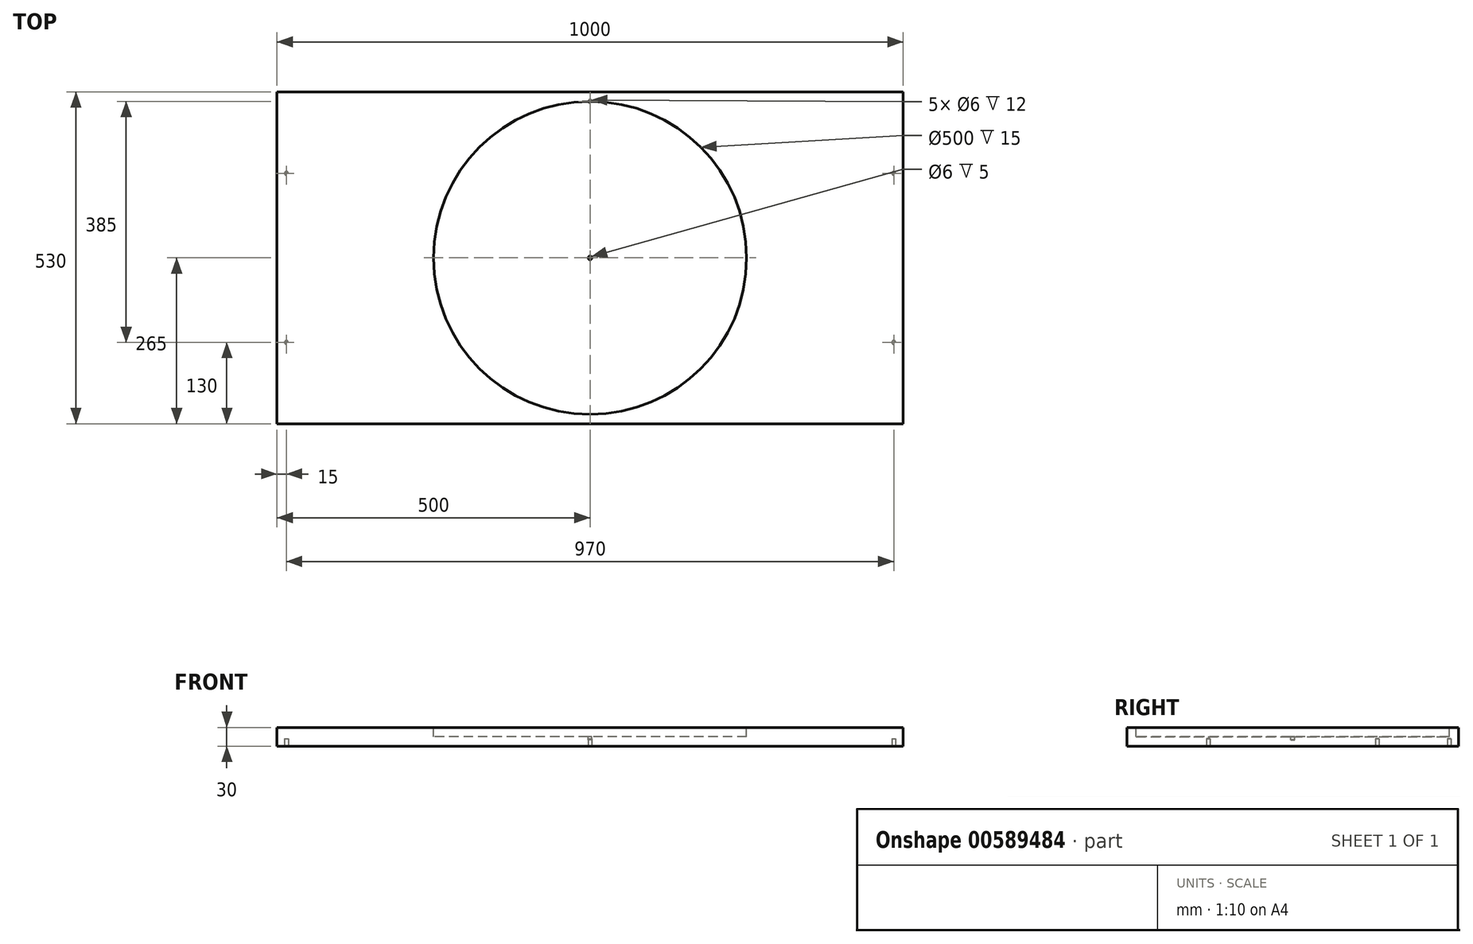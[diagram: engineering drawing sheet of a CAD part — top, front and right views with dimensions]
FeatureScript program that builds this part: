
annotation { "Feature Type Name" : "Feature", "Feature Type Description" : "" }
export const myFeature = defineFeature(function(context is Context, id is Id, definition is map)
    precondition{}
    {
        {
            var Q0;
            Q0=qCreatedBy(makeId("Top.planeOp"),FACE);
            var sketch = newSketch(context, id + "F0", { "sketchPlane" : qUnion([Q0])});
            skLineSegment(sketch, "E0.bottom", {"start": v(0, 0) * mm, "end": v(1000, 0) * mm});
            skLineSegment(sketch, "E0.top", {"start": v(0, 530) * mm, "end": v(1000, 530) * mm});
            skLineSegment(sketch, "E0.left", {"start": v(0, 0) * mm, "end": v(0, 530) * mm});
            skLineSegment(sketch, "E0.right", {"start": v(1000, 0) * mm, "end": v(1000, 530) * mm});
            skSolve(sketch);
        }
        {
            var Q0;
            Q0=makeQuery(id+"F0.imprint","IMPRINT",FACE,{"disambiguationData":[TD([[makeQuery(id+"F0.imprint","IMPRINT",EDGE,{"derivedFrom":sQuery(id+"F0.wireOp",EDGE,"E0.bottom")}),1.0]])]});
            extrude(context, id + "F1", {"entities" : qUnion([Q0]), "depth" : 30 * mm, "offsetDistance" : 25 * mm});
        }
        {
            var Q0;
            Q0=makeQuery(id+"F1.opExtrude","CAP_FACE",FACE,{"disambiguationData":[OSD([sQuery(id+"F0.wireOp",EDGE,"E0.bottom"),sQuery(id+"F0.wireOp",EDGE,"E0.top"),sQuery(id+"F0.wireOp",EDGE,"E0.left"),sQuery(id+"F0.wireOp",EDGE,"E0.right")])],"isStart":true});
            var sketch = newSketch(context, id + "F2", { "sketchPlane" : qUnion([Q0])});
            skCircle(sketch, "E1", {"center": v(985, -130) * mm, "radius": 3 * mm});
            skSolve(sketch);
        }
        {
            var Q0;
            Q0=makeQuery(id+"F2.imprint","IMPRINT",FACE,{"disambiguationData":[TD([[makeQuery(id+"F2.imprint","IMPRINT",EDGE,{"derivedFrom":sQuery(id+"F2.wireOp",EDGE,"E1")}),1.0]])]});
            extrude(context, id + "F3", {"entities" : qUnion([Q0]), "operationType" : NewBodyOperationType.REMOVE, "oppositeDirection" : true, "depth" : 12 * mm, "offsetDistance" : 25 * mm});
        }
        {
            var Q0;
            Q0=makeQuery(id+"F1.opExtrude","CAP_FACE",FACE,{"disambiguationData":[OSD([sQuery(id+"F0.wireOp",EDGE,"E0.bottom"),sQuery(id+"F0.wireOp",EDGE,"E0.top"),sQuery(id+"F0.wireOp",EDGE,"E0.left"),sQuery(id+"F0.wireOp",EDGE,"E0.right")])],"isStart":true});
            var sketch = newSketch(context, id + "F4", { "sketchPlane" : qUnion([Q0])});
            skCircle(sketch, "E2", {"center": v(15, -130) * mm, "radius": 3 * mm});
            skCircle(sketch, "E3", {"center": v(15, -400) * mm, "radius": 3 * mm});
            skSolve(sketch);
        }
        {
            var Q0;
            Q0=makeQuery(id+"F4.imprint","IMPRINT",FACE,{"disambiguationData":[TD([[makeQuery(id+"F4.imprint","IMPRINT",EDGE,{"derivedFrom":sQuery(id+"F4.wireOp",EDGE,"E2")}),1.0]])]});
            extrude(context, id + "F5", {"entities" : qUnion([Q0]), "operationType" : NewBodyOperationType.REMOVE, "oppositeDirection" : true, "depth" : 12 * mm, "offsetDistance" : 25 * mm});
        }
        {
            var Q0;
            Q0=makeQuery(id+"F1.opExtrude","CAP_FACE",FACE,{"disambiguationData":[OSD([sQuery(id+"F0.wireOp",EDGE,"E0.bottom"),sQuery(id+"F0.wireOp",EDGE,"E0.top"),sQuery(id+"F0.wireOp",EDGE,"E0.left"),sQuery(id+"F0.wireOp",EDGE,"E0.right")])],"isStart":false});
            var sketch = newSketch(context, id + "F6", { "sketchPlane" : qUnion([Q0])});
            skCircle(sketch, "E4", {"center": v(500, 265) * mm, "radius": 250 * mm});
            skPoint(sketch, "E4.centerSnap0", {"position": v(0, 265) * mm});
            skPoint(sketch, "E4.centerSnap1", {"position": v(500, 530) * mm});
            skSolve(sketch);
        }
        {
            var Q0;
            Q0=makeQuery(id+"F1.opExtrude","CAP_FACE",FACE,{"disambiguationData":[OSD([sQuery(id+"F0.wireOp",EDGE,"E0.bottom"),sQuery(id+"F0.wireOp",EDGE,"E0.top"),sQuery(id+"F0.wireOp",EDGE,"E0.left"),sQuery(id+"F0.wireOp",EDGE,"E0.right")])],"isStart":true});
            var sketch = newSketch(context, id + "F7", { "sketchPlane" : qUnion([Q0])});
            skCircle(sketch, "E5", {"center": v(985, -400) * mm, "radius": 3 * mm});
            skSolve(sketch);
        }
        {
            var Q0;
            Q0=makeQuery(id+"F7.imprint","IMPRINT",FACE,{"disambiguationData":[TD([[makeQuery(id+"F7.imprint","IMPRINT",EDGE,{"derivedFrom":sQuery(id+"F7.wireOp",EDGE,"E5")}),1.0]])]});
            extrude(context, id + "F8", {"entities" : qUnion([Q0]), "operationType" : NewBodyOperationType.REMOVE, "oppositeDirection" : true, "depth" : 12 * mm, "offsetDistance" : 25 * mm});
        }
        {
            var Q0;
            Q0=makeQuery(id+"F1.opExtrude","CAP_FACE",FACE,{"disambiguationData":[OSD([sQuery(id+"F0.wireOp",EDGE,"E0.bottom"),sQuery(id+"F0.wireOp",EDGE,"E0.top"),sQuery(id+"F0.wireOp",EDGE,"E0.left"),sQuery(id+"F0.wireOp",EDGE,"E0.right")])],"isStart":true});
            var sketch = newSketch(context, id + "F9", { "sketchPlane" : qUnion([Q0])});
            skCircle(sketch, "E6", {"center": v(15, -400) * mm, "radius": 3 * mm});
            skSolve(sketch);
        }
        {
            var Q0;
            Q0=makeQuery(id+"F9.imprint","IMPRINT",FACE,{"disambiguationData":[TD([[makeQuery(id+"F9.imprint","IMPRINT",EDGE,{"derivedFrom":sQuery(id+"F9.wireOp",EDGE,"E6")}),1.0]])]});
            extrude(context, id + "F10", {"entities" : qUnion([Q0]), "operationType" : NewBodyOperationType.REMOVE, "oppositeDirection" : true, "depth" : 12 * mm, "offsetDistance" : 25 * mm});
        }
        {
            var Q0;
            Q0=makeQuery(id+"F6.imprint","IMPRINT",FACE,{"disambiguationData":[TD([[makeQuery(id+"F6.imprint","IMPRINT",EDGE,{"derivedFrom":sQuery(id+"F6.wireOp",EDGE,"E4")}),1.0]])]});
            extrude(context, id + "F11", {"entities" : qUnion([Q0]), "operationType" : NewBodyOperationType.REMOVE, "oppositeDirection" : true, "depth" : 15 * mm, "offsetDistance" : 25 * mm});
        }
        {
            var Q0;
            Q0=makeQuery(id+"F11.boolean.opBoolean","COPY",FACE,{"derivedFrom":makeQuery(id+"F11.opExtrude","CAP_FACE",FACE,{"disambiguationData":[OSD([sQuery(id+"F6.wireOp",EDGE,"E4")])],"isStart":false})});
            var sketch = newSketch(context, id + "F12", { "sketchPlane" : qUnion([Q0])});
            skCircle(sketch, "E7", {"center": v(500, 265) * mm, "radius": 3 * mm});
            skSolve(sketch);
        }
        {
            var Q0;
            Q0=makeQuery(id+"F12.imprint","IMPRINT",FACE,{"disambiguationData":[TD([[makeQuery(id+"F12.imprint","IMPRINT",EDGE,{"derivedFrom":sQuery(id+"F12.wireOp",EDGE,"E7")}),1.0]])]});
            extrude(context, id + "F13", {"entities" : qUnion([Q0]), "operationType" : NewBodyOperationType.REMOVE, "oppositeDirection" : true, "depth" : 5 * mm, "offsetDistance" : 25 * mm});
        }
        {
            var Q0;
            Q0=makeQuery(id+"F1.opExtrude","CAP_FACE",FACE,{"disambiguationData":[OSD([sQuery(id+"F0.wireOp",EDGE,"E0.bottom"),sQuery(id+"F0.wireOp",EDGE,"E0.top"),sQuery(id+"F0.wireOp",EDGE,"E0.left"),sQuery(id+"F0.wireOp",EDGE,"E0.right")])],"isStart":true});
            var sketch = newSketch(context, id + "F14", { "sketchPlane" : qUnion([Q0])});
            skCircle(sketch, "E8", {"center": v(500, -515) * mm, "radius": 3 * mm});
            skPoint(sketch, "E8.centerSnap0", {"position": v(500, -530) * mm});
            skSolve(sketch);
        }
        {
            var Q0;
            Q0=makeQuery(id+"F14.imprint","IMPRINT",FACE,{"disambiguationData":[TD([[makeQuery(id+"F14.imprint","IMPRINT",EDGE,{"derivedFrom":sQuery(id+"F14.wireOp",EDGE,"E8")}),1.0]])]});
            extrude(context, id + "F15", {"entities" : qUnion([Q0]), "operationType" : NewBodyOperationType.REMOVE, "oppositeDirection" : true, "depth" : 12 * mm, "offsetDistance" : 25 * mm});
        }
    });
